# Revit family: Faucet-Wall_Mount-Lavatory-KOHLER-REFINED-K-22570T_1
name_source: partatom
category: Plumbing Fixtures
revit_build: Autodesk Revit 2017 (Build: 20160225_1515(x64)
units: mm (PartAtom-declared; Revit-internal decimal feet)

## family parameters
Cut with Voids When Loaded = No
Host = Face
OmniClass Number = 23.31.11.00
OmniClass Title = Faucets
Part Type = Normal
Room Calculation Point = No
Round Connector Dimension = Use Diameter
Shared = No

## types (5) — shared parameters
ADA Compliant = No
Assembly Code = D2010
CW Connection = Yes
Cold Water Inlet = Cold Water Inlet
Date Modified = 06/22/2020
Default Elevation = 36"
Description = Ruofang double-handle faucet with wall outlet (outlet nozzle length 218mm)
Drain Included = Yes
Faucet Hole Spacing = 7 15/16"
Flow Rate = 2 GPM
HW Connection = Yes
Handle Clearance = 2 7/16"
Height = 2"
Hot Water Inlet = Hot Water Inlet
Length = 8 9/16"
Manufacturer = KOHLER Co.
Master Format 2014 = 22 41 39
Master Format 2014 Name = Residential Faucets, Supplies, and Trim
Material = Premium Metal Construction
Pressure = 45.00 psi
Product Documentation Link = https://files.kohler.com.cn
Product Name = REFINED
Product Page URL = https://www.kohler.com.cn
Spout Reach = 8 9/16"
URL = http://www.kohler.com.cn
Vent Connection = No
Waste Connection = No
Waste Water Outlet = Waste Water Outlet
WaterSense Certified = No
Width = 7 15/16"

## per-type parameters (varying)
| type | Finish | Model | Type |
| CP-Polished Chrome | Kohler-Metal-CP-Polished_Chrome | K-22570T-4-CP | 1 |
| AF-Flange Gold | Kohler-Metal-AF-Flange_Gold | K-22570T-4-AF | 2 |
| BN-Roman Silver | Kohler-Metal-BN-Roman_Silver | K-22570T-4-BN | 3 |
| RGD-Rose Gold | Kohler-Metal-RGD-Rose_Gold | K-22570T-4-RGD | 4 |
| BL-Primary Black | Kohler-Metal-BL-Matte_Black | K-22570T-4-BL | 5 |

## geometry (parser evidence)
native form markers: Sweep x3
no freeform markers — native parametric forms only
